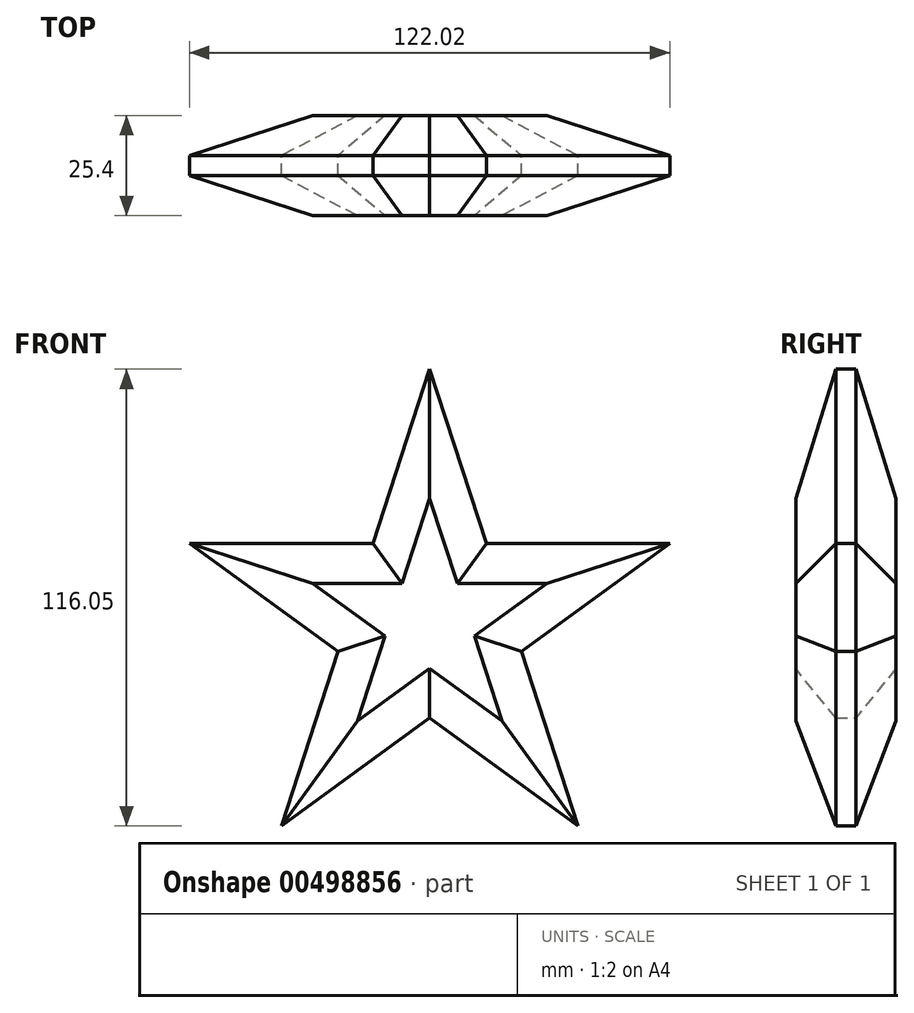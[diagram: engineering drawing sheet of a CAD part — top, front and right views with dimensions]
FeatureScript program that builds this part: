
annotation { "Feature Type Name" : "Feature", "Feature Type Description" : "" }
export const myFeature = defineFeature(function(context is Context, id is Id, definition is map)
    precondition{}
    {
        {
            var Q0;
            Q0=qCreatedBy(makeId("Front.planeOp"),FACE);
            var sketch = newSketch(context, id + "F0", { "sketchPlane" : qUnion([Q0])});
            skCircle(sketch, "E0.cCircle", {"center": v(0, 0) * mm, "radius": 51.9 * mm, "construction": true});
            skLineSegment(sketch, "E0.0", {"start": v(37.7, -51.9) * mm, "end": v(-37.7, -51.9) * mm, "construction": true});
            skLineSegment(sketch, "E0.1", {"start": v(-37.7, -51.9) * mm, "end": v(-61, 19.82) * mm, "construction": true});
            skLineSegment(sketch, "E0.2", {"start": v(-61, 19.82) * mm, "end": v(0, 64.15) * mm, "construction": true});
            skLineSegment(sketch, "E0.3", {"start": v(0, 64.15) * mm, "end": v(61, 19.82) * mm, "construction": true});
            skLineSegment(sketch, "E0.4", {"start": v(61, 19.82) * mm, "end": v(37.7, -51.9) * mm, "construction": true});
            skPoint(sketch, "E0.0.midPoint", {"position": v(0, -51.9) * mm});
            skLineSegment(sketch, "E1", {"start": v(0, 64.15) * mm, "end": v(-14.4, 19.82) * mm});
            skLineSegment(sketch, "E2", {"start": v(-37.7, -51.9) * mm, "end": v(0, -24.5) * mm});
            skLineSegment(sketch, "E3", {"start": v(61, 19.82) * mm, "end": v(14.4, 19.82) * mm});
            skLineSegment(sketch, "E4", {"start": v(-61, 19.82) * mm, "end": v(-23.3, -7.57) * mm});
            skLineSegment(sketch, "E5", {"start": v(37.7, -51.9) * mm, "end": v(23.3, -7.57) * mm});
            skLineSegment(sketch, "E6.trimOffspring", {"start": v(-14.4, 19.82) * mm, "end": v(-61, 19.82) * mm});
            skLineSegment(sketch, "E7.trimOffspring", {"start": v(-23.3, -7.57) * mm, "end": v(-37.7, -51.9) * mm});
            skLineSegment(sketch, "E8.trimOffspring", {"start": v(0, -24.5) * mm, "end": v(37.7, -51.9) * mm});
            skLineSegment(sketch, "E9.trimOffspring", {"start": v(23.3, -7.57) * mm, "end": v(61, 19.82) * mm});
            skLineSegment(sketch, "E10.trimOffspring", {"start": v(14.4, 19.82) * mm, "end": v(0, 64.15) * mm});
            skSolve(sketch);
        }
        {
            var Q0;
            Q0=makeQuery(id+"F0.imprint","IMPRINT",FACE,{"disambiguationData":[TD([[makeQuery(id+"F0.imprint","IMPRINT",EDGE,{"derivedFrom":sQuery(id+"F0.wireOp",EDGE,"E1")}),1.0]])]});
            extrude(context, id + "F1", {"entities" : qUnion([Q0]), "depth" : 25.4 * mm, "offsetDistance" : 25.4 * mm});
        }
        {
            var Q0;
            Q0=makeQuery(id+"F1.opExtrude","CAP_FACE",FACE,{"disambiguationData":[OSD([sQuery(id+"F0.wireOp",EDGE,"E1"),sQuery(id+"F0.wireOp",EDGE,"E2"),sQuery(id+"F0.wireOp",EDGE,"E3"),sQuery(id+"F0.wireOp",EDGE,"E4"),sQuery(id+"F0.wireOp",EDGE,"E5"),sQuery(id+"F0.wireOp",EDGE,"E6.trimOffspring"),sQuery(id+"F0.wireOp",EDGE,"E7.trimOffspring"),sQuery(id+"F0.wireOp",EDGE,"E8.trimOffspring"),sQuery(id+"F0.wireOp",EDGE,"E9.trimOffspring"),sQuery(id+"F0.wireOp",EDGE,"E10.trimOffspring")])],"isStart":false});
            var Q1;
            Q1=makeQuery(id+"F1.opExtrude","CAP_FACE",FACE,{"disambiguationData":[OSD([sQuery(id+"F0.wireOp",EDGE,"E1"),sQuery(id+"F0.wireOp",EDGE,"E2"),sQuery(id+"F0.wireOp",EDGE,"E3"),sQuery(id+"F0.wireOp",EDGE,"E4"),sQuery(id+"F0.wireOp",EDGE,"E5"),sQuery(id+"F0.wireOp",EDGE,"E6.trimOffspring"),sQuery(id+"F0.wireOp",EDGE,"E7.trimOffspring"),sQuery(id+"F0.wireOp",EDGE,"E8.trimOffspring"),sQuery(id+"F0.wireOp",EDGE,"E9.trimOffspring"),sQuery(id+"F0.wireOp",EDGE,"E10.trimOffspring")])],"isStart":true});
            chamfer(context, id + "F2", {"entities" : qUnion([Q0, Q1]), "width" : 10.16 * mm, "tangentPropagation" : true});
        }
    });
